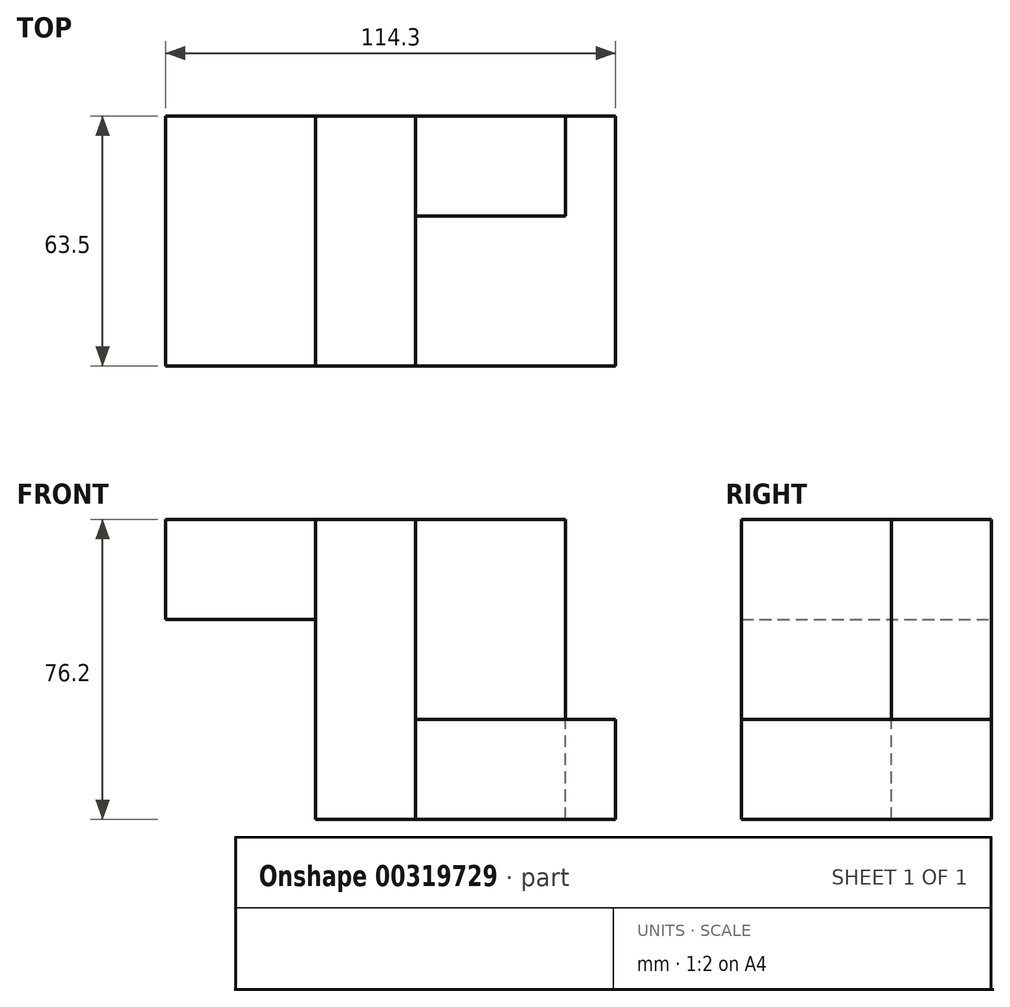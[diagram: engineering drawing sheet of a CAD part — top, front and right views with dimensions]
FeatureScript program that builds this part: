
annotation { "Feature Type Name" : "Feature", "Feature Type Description" : "" }
export const myFeature = defineFeature(function(context is Context, id is Id, definition is map)
    precondition{}
    {
        {
            var Q0;
            Q0=qCreatedBy(makeId("Top.planeOp"),FACE);
            var sketch = newSketch(context, id + "F0", { "sketchPlane" : qUnion([Q0])});
            skLineSegment(sketch, "E0", {"start": v(-44.05, 41.83) * mm, "end": v(57.55, 41.83) * mm});
            skLineSegment(sketch, "E1", {"start": v(57.55, 41.83) * mm, "end": v(57.55, 16.43) * mm});
            skLineSegment(sketch, "E2", {"start": v(57.55, 16.43) * mm, "end": v(19.45, 16.43) * mm});
            skLineSegment(sketch, "E3", {"start": v(19.45, 16.43) * mm, "end": v(19.45, -21.67) * mm});
            skLineSegment(sketch, "E4", {"start": v(19.45, -21.67) * mm, "end": v(-44.05, -21.67) * mm});
            skLineSegment(sketch, "E5", {"start": v(-44.05, -21.67) * mm, "end": v(-44.05, 41.83) * mm});
            skLineSegment(sketch, "E6", {"start": v(19.45, 16.43) * mm, "end": v(19.45, 41.83) * mm});
            skPoint(sketch, "E6.endSnap0", {"position": v(6.75, 41.83) * mm});
            skLineSegment(sketch, "E7", {"start": v(19.45, 41.83) * mm, "end": v(57.55, 41.83) * mm});
            skLineSegment(sketch, "E8", {"start": v(-5.95, -21.67) * mm, "end": v(-5.95, 41.83) * mm});
            skLineSegment(sketch, "E9", {"start": v(-5.95, -21.67) * mm, "end": v(19.45, -21.67) * mm});
            skLineSegment(sketch, "E10", {"start": v(19.45, 41.83) * mm, "end": v(-5.95, 41.83) * mm});
            skLineSegment(sketch, "E11", {"start": v(19.45, 16.43) * mm, "end": v(57.55, 16.43) * mm});
            skLineSegment(sketch, "E12", {"start": v(70.25, -21.67) * mm, "end": v(19.45, -21.67) * mm});
            skLineSegment(sketch, "E13", {"start": v(70.25, -21.67) * mm, "end": v(70.25, 16.43) * mm});
            skLineSegment(sketch, "E14", {"start": v(70.25, 16.43) * mm, "end": v(70.25, 41.83) * mm});
            skLineSegment(sketch, "E15", {"start": v(70.25, 41.83) * mm, "end": v(57.55, 41.83) * mm});
            skSolve(sketch);
        }
        {
            var Q0;
            Q0=makeQuery(id+"F0.imprint","IMPRINT",FACE,{"disambiguationData":[TD([[makeQuery(id+"F0.imprint","IMPRINT",EDGE,{"derivedFrom":sQuery(id+"F0.wireOp",EDGE,"E0")}),-1.0]])]});
            extrude(context, id + "F1", {"entities" : qUnion([Q0]), "oppositeDirection" : true, "depth" : 25.4 * mm});
        }
        {
            var Q0;
            Q0=makeQuery(id+"F0.imprint","IMPRINT",FACE,{"disambiguationData":[TD([[makeQuery(id+"F0.imprint","IMPRINT",EDGE,{"derivedFrom":sQuery(id+"F0.wireOp",EDGE,"E1")}),-1.0]])]});
            extrude(context, id + "F2", {"entities" : qUnion([Q0]), "operationType" : NewBodyOperationType.ADD, "oppositeDirection" : true, "depth" : 76.2 * mm});
        }
        {
            var Q0;
            Q0=makeQuery(id+"F0.imprint","IMPRINT",FACE,{"disambiguationData":[TD([[makeQuery(id+"F0.imprint","IMPRINT",EDGE,{"derivedFrom":sQuery(id+"F0.wireOp",EDGE,"E3")}),-1.0]])]});
            extrude(context, id + "F3", {"entities" : qUnion([Q0]), "oppositeDirection" : true, "depth" : 76.2 * mm});
        }
        {
            var Q0;
            Q0=makeQuery(id+"F0.imprint","IMPRINT",FACE,{"disambiguationData":[TD([[makeQuery(id+"F0.imprint","IMPRINT",EDGE,{"derivedFrom":sQuery(id+"F0.wireOp",EDGE,"E3")}),1.0]])]});
            extrude(context, id + "F4", {"entities" : qUnion([Q0]), "oppositeDirection" : true, "depth" : 76.2 * mm});
        }
        {
            var Q0;
            Q0=makeQuery(id+"F0.imprint","IMPRINT",FACE,{"disambiguationData":[TD([[makeQuery(id+"F0.imprint","IMPRINT",EDGE,{"derivedFrom":sQuery(id+"F0.wireOp",EDGE,"E3")}),1.0]])]});
            extrude(context, id + "F5", {"entities" : qUnion([Q0]), "operationType" : NewBodyOperationType.REMOVE, "oppositeDirection" : true, "depth" : 50.8 * mm});
        }
    });
